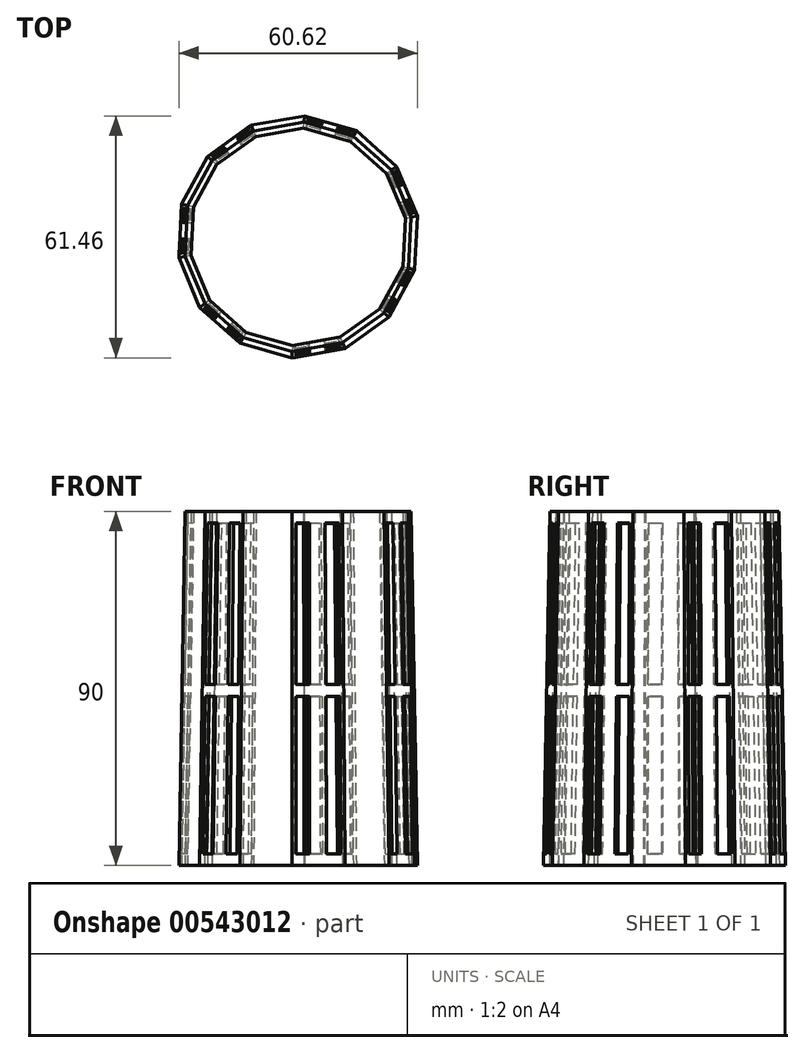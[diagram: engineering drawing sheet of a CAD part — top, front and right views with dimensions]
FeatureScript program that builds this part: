
annotation { "Feature Type Name" : "Feature", "Feature Type Description" : "" }
export const myFeature = defineFeature(function(context is Context, id is Id, definition is map)
    precondition{}
    {
        {
            var Q0;
            Q0=qCreatedBy(makeId("Top.planeOp"),FACE);
            var sketch = newSketch(context, id + "F0", { "sketchPlane" : qUnion([Q0])});
            skCircle(sketch, "E0.cCircle", {"center": v(0, 0) * mm, "radius": 30 * mm, "construction": true});
            skLineSegment(sketch, "E0.0", {"start": v(-25.01, -17.92) * mm, "end": v(-30.31, -5.3) * mm});
            skLineSegment(sketch, "E0.1", {"start": v(-30.31, -5.3) * mm, "end": v(-29.6, 8.38) * mm});
            skLineSegment(sketch, "E0.2", {"start": v(-29.6, 8.38) * mm, "end": v(-23.04, 20.4) * mm});
            skLineSegment(sketch, "E0.3", {"start": v(-23.04, 20.4) * mm, "end": v(-11.9, 28.37) * mm});
            skLineSegment(sketch, "E0.4", {"start": v(-11.9, 28.37) * mm, "end": v(1.58, 30.73) * mm});
            skLineSegment(sketch, "E0.5", {"start": v(1.58, 30.73) * mm, "end": v(14.76, 27) * mm});
            skLineSegment(sketch, "E0.6", {"start": v(14.76, 27) * mm, "end": v(25.01, 17.92) * mm});
            skLineSegment(sketch, "E0.7", {"start": v(25.01, 17.92) * mm, "end": v(30.31, 5.3) * mm});
            skLineSegment(sketch, "E0.8", {"start": v(30.31, 5.3) * mm, "end": v(29.6, -8.38) * mm});
            skLineSegment(sketch, "E0.9", {"start": v(29.6, -8.38) * mm, "end": v(23.04, -20.4) * mm});
            skLineSegment(sketch, "E0.10", {"start": v(23.04, -20.4) * mm, "end": v(11.9, -28.37) * mm});
            skLineSegment(sketch, "E0.11", {"start": v(11.9, -28.37) * mm, "end": v(-1.58, -30.73) * mm});
            skLineSegment(sketch, "E0.12", {"start": v(-1.58, -30.73) * mm, "end": v(-14.76, -27) * mm});
            skLineSegment(sketch, "E0.13", {"start": v(-14.76, -27) * mm, "end": v(-25.01, -17.92) * mm});
            skPoint(sketch, "E0.0.midPoint", {"position": v(-27.66, -11.61) * mm});
            skSolve(sketch);
        }
        {
            var Q0;
            Q0=makeQuery(id+"F0.imprint","IMPRINT",FACE,{"disambiguationData":[TD([[makeQuery(id+"F0.imprint","IMPRINT",EDGE,{"derivedFrom":sQuery(id+"F0.wireOp",EDGE,"E0.0")}),-1.0]])]});
            extrude(context, id + "F1", {"entities" : qUnion([Q0]), "depth" : 90 * mm, "offsetDistance" : 25 * mm, "hasDraft" : true, "draftAngle" : 1 * degree, "draftPullDirection" : true});
        }
        {
            var Q0;
            Q0=makeQuery(id+"F1.opExtrude","CAP_FACE",FACE,{"disambiguationData":[OSD([sQuery(id+"F0.wireOp",EDGE,"E0.0"),sQuery(id+"F0.wireOp",EDGE,"E0.1"),sQuery(id+"F0.wireOp",EDGE,"E0.2"),sQuery(id+"F0.wireOp",EDGE,"E0.3"),sQuery(id+"F0.wireOp",EDGE,"E0.4"),sQuery(id+"F0.wireOp",EDGE,"E0.5"),sQuery(id+"F0.wireOp",EDGE,"E0.6"),sQuery(id+"F0.wireOp",EDGE,"E0.7"),sQuery(id+"F0.wireOp",EDGE,"E0.8"),sQuery(id+"F0.wireOp",EDGE,"E0.9"),sQuery(id+"F0.wireOp",EDGE,"E0.10"),sQuery(id+"F0.wireOp",EDGE,"E0.11"),sQuery(id+"F0.wireOp",EDGE,"E0.12"),sQuery(id+"F0.wireOp",EDGE,"E0.13")])],"isStart":false});
            var Q1;
            Q1=makeQuery(id+"F1.opExtrude","CAP_FACE",FACE,{"disambiguationData":[OSD([sQuery(id+"F0.wireOp",EDGE,"E0.0"),sQuery(id+"F0.wireOp",EDGE,"E0.1"),sQuery(id+"F0.wireOp",EDGE,"E0.2"),sQuery(id+"F0.wireOp",EDGE,"E0.3"),sQuery(id+"F0.wireOp",EDGE,"E0.4"),sQuery(id+"F0.wireOp",EDGE,"E0.5"),sQuery(id+"F0.wireOp",EDGE,"E0.6"),sQuery(id+"F0.wireOp",EDGE,"E0.7"),sQuery(id+"F0.wireOp",EDGE,"E0.8"),sQuery(id+"F0.wireOp",EDGE,"E0.9"),sQuery(id+"F0.wireOp",EDGE,"E0.10"),sQuery(id+"F0.wireOp",EDGE,"E0.11"),sQuery(id+"F0.wireOp",EDGE,"E0.12"),sQuery(id+"F0.wireOp",EDGE,"E0.13")])],"isStart":true});
            shell(context, id + "F2", {"entities" : qUnion([Q0, Q1]), "thickness" : 1.5 * mm});
        }
        {
            var Q0;
            Q0=makeQuery(id+"F1.opExtrude","SWEPT_FACE",FACE,{"disambiguationData":[OSD([sQuery(id+"F0.wireOp",EDGE,"E0.1")])]});
            var sketch = newSketch(context, id + "F3", { "sketchPlane" : qUnion([Q0])});
            skLineSegment(sketch, "E1.bottom", {"start": v(5.58, 86.49) * mm, "end": v(2.08, 86.49) * mm});
            skLineSegment(sketch, "E1.top", {"start": v(5.7, 45.49) * mm, "end": v(2.08, 45.49) * mm});
            skLineSegment(sketch, "E1.left", {"start": v(5.58, 86.49) * mm, "end": v(5.7, 45.49) * mm});
            skLineSegment(sketch, "E1.right", {"start": v(2.08, 86.49) * mm, "end": v(2.08, 45.49) * mm});
            skLineSegment(sketch, "E2.bottom", {"start": v(5.71, 42.49) * mm, "end": v(2.08, 42.49) * mm});
            skLineSegment(sketch, "E2.top", {"start": v(5.84, 2.47) * mm, "end": v(2.08, 2.47) * mm});
            skLineSegment(sketch, "E2.left", {"start": v(5.71, 42.49) * mm, "end": v(5.84, 2.47) * mm});
            skLineSegment(sketch, "E2.right", {"start": v(2.08, 42.49) * mm, "end": v(2.08, 2.47) * mm});
            skLineSegment(sketch, "E3.bottom", {"start": v(-2.14, 42.49) * mm, "end": v(-5.64, 42.5) * mm});
            skLineSegment(sketch, "E3.top", {"start": v(-2.33, 2.48) * mm, "end": v(-5.83, 2.48) * mm});
            skLineSegment(sketch, "E3.left", {"start": v(-2.14, 42.49) * mm, "end": v(-2.33, 2.48) * mm});
            skLineSegment(sketch, "E3.right", {"start": v(-5.64, 42.5) * mm, "end": v(-5.83, 2.48) * mm});
            skLineSegment(sketch, "E4.bottom", {"start": v(-1.92, 86.5) * mm, "end": v(-5.42, 86.5) * mm});
            skLineSegment(sketch, "E4.top", {"start": v(-2.12, 45.49) * mm, "end": v(-5.62, 45.5) * mm});
            skLineSegment(sketch, "E4.left", {"start": v(-1.92, 86.5) * mm, "end": v(-2.12, 45.49) * mm});
            skLineSegment(sketch, "E4.right", {"start": v(-5.42, 86.5) * mm, "end": v(-5.62, 45.5) * mm});
            skLineSegment(sketch, "E5", {"start": v(5.84, 2.47) * mm, "end": v(6.84, 2.47) * mm, "construction": true});
            skLineSegment(sketch, "E6", {"start": v(5.84, 2.47) * mm, "end": v(5.85, -0.53) * mm, "construction": true});
            skLineSegment(sketch, "E7", {"start": v(5.58, 86.49) * mm, "end": v(5.57, 89.49) * mm, "construction": true});
            skLineSegment(sketch, "E8", {"start": v(5.58, 86.49) * mm, "end": v(6.58, 86.48) * mm, "construction": true});
            skLineSegment(sketch, "E9", {"start": v(5.71, 42.49) * mm, "end": v(5.7, 45.49) * mm, "construction": true});
            skLineSegment(sketch, "E10", {"start": v(2.08, 42.49) * mm, "end": v(2.08, 45.49) * mm, "construction": true});
            skLineSegment(sketch, "E11", {"start": v(-5.42, 86.5) * mm, "end": v(-5.4, 89.5) * mm, "construction": true});
            skLineSegment(sketch, "E12", {"start": v(-5.42, 86.5) * mm, "end": v(-6.42, 86.5) * mm, "construction": true});
            skLineSegment(sketch, "E13", {"start": v(-5.83, 2.48) * mm, "end": v(-5.85, -0.52) * mm, "construction": true});
            skLineSegment(sketch, "E14", {"start": v(-5.83, 2.48) * mm, "end": v(-6.83, 2.48) * mm, "construction": true});
            skLineSegment(sketch, "E15", {"start": v(-2.14, 42.49) * mm, "end": v(-2.12, 45.49) * mm, "construction": true});
            skLineSegment(sketch, "E16", {"start": v(-5.64, 42.5) * mm, "end": v(-5.62, 45.5) * mm, "construction": true});
            skSolve(sketch);
        }
        {
            var Q0;
            Q0=qCreatedBy(makeId("Front.planeOp"),FACE);
            var sketch = newSketch(context, id + "F4", { "sketchPlane" : qUnion([Q0])});
            skLineSegment(sketch, "E17", {"start": v(0, 0) * mm, "end": v(0, 100) * mm});
            skSolve(sketch);
        }
        {
            var Q0;
            Q0 = qSketchRegion(id + "F3", true);
            extrude(context, id + "F5", {"entities" : qUnion([Q0]), "endBound" : BoundingType.UP_TO_NEXT, "oppositeDirection" : true, "depth" : 25 * mm, "offsetDistance" : 25 * mm});
        }
        {
            var Q0;
            Q0=makeQuery(id+"F5.opExtrude","SWEPT_BODY",BODY,{"disambiguationData":[OSD([sQuery(id+"F3.wireOp",EDGE,"E1.bottom"),sQuery(id+"F3.wireOp",EDGE,"E1.top"),sQuery(id+"F3.wireOp",EDGE,"E1.left"),sQuery(id+"F3.wireOp",EDGE,"E1.right")])]});
            var Q1;
            Q1=makeQuery(id+"F5.opExtrude","SWEPT_BODY",BODY,{"disambiguationData":[OSD([sQuery(id+"F3.wireOp",EDGE,"E2.bottom"),sQuery(id+"F3.wireOp",EDGE,"E2.top"),sQuery(id+"F3.wireOp",EDGE,"E2.left"),sQuery(id+"F3.wireOp",EDGE,"E2.right")])]});
            var Q2;
            Q2=makeQuery(id+"F5.opExtrude","SWEPT_BODY",BODY,{"disambiguationData":[OSD([sQuery(id+"F3.wireOp",EDGE,"E3.bottom"),sQuery(id+"F3.wireOp",EDGE,"E3.top"),sQuery(id+"F3.wireOp",EDGE,"E3.left"),sQuery(id+"F3.wireOp",EDGE,"E3.right")])]});
            var Q3;
            Q3=makeQuery(id+"F5.opExtrude","SWEPT_BODY",BODY,{"disambiguationData":[OSD([sQuery(id+"F3.wireOp",EDGE,"E4.bottom"),sQuery(id+"F3.wireOp",EDGE,"E4.top"),sQuery(id+"F3.wireOp",EDGE,"E4.left"),sQuery(id+"F3.wireOp",EDGE,"E4.right")])]});
            var Q4;
            Q4=sQuery(id+"F4.wireOp",EDGE,"E17");
            circularPattern(context, id + "F6", {"operationType" : NewBodyOperationType.REMOVE, "entities" : qUnion([Q0, Q1, Q2, Q3]), "axis" : qUnion([Q4]), "angle" : 360 * degree, "instanceCount" : 7, "equalSpace" : true});
        }
    });
